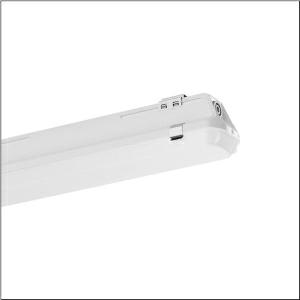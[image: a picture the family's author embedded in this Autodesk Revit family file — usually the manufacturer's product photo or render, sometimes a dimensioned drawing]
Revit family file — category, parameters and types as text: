
# Revit family: monsun_r__11_51fp10mp4b0q_f78f
name_source: partatom
category: Lighting Fixtures
units: mm (PartAtom-declared; Revit-internal decimal feet)

## family parameters
Cut with Voids When Loaded = No
Host = Face
Light Source = No
Part Type = Normal
Room Calculation Point = No
Round Connector Dimension = Use Diameter
Shared = No

## types (1)
- --- (1 x LED, 12070 lm, 66.2 W, 4000K)
    Apparent Load = 66 VA
    CIE Flux Codes = 47 76 93 94 100
    Color Rendering = 80
    Color Temperature = 4000K
    Default Elevation = 1800 mm
    Description = Monsun® 11, damp-proof luminaire, chain hanger, primary optical cover: enclosure, of PMMA, light emission: direct distribution, primary light characteristic: symmetric, installation type: suspended mounting, surface-mounted, horizontal mounting, vertical mounting, LED, rated luminous flux: 12.070lm, luminous efficacy: 182lm/W, light colour: 840, colour temperature: 4000K, control gear: ECG, with terminal, 3-pole, max. 2.5mm², mains connection: 220..240V, AC, 50/60Hz, rated input power: 66W, luminaire housing, of glass-fibre reinforced polyester, uncoated, bright grey, incl. chain hanger, length: 1.590mm, width: 90mm, height: 88mm, clip for enclosure, of stainless steel (V2A), ceiling mounting element, of stainless steel (V2A), chain hanger, of stainless steel (V2A), protection rating (complete): IP66, insulation class (complete): insulation class I (protective earthing), certification: CE, ENEC, VDE, UKCA, protection symbol: D, impact resistance: IK04, permissible operating ambient temperature: -35..+35°C, standard: EN 50419, EN 60598-2-1, no direct snow, no direct sun, no direct rain, for indoor or canopied outdoor use, corresponds to IFS (International Featured Standards) requirements for safety and quality in the food industry, contact your sales advisor before using the luminaires in applications with unclear chemical exposure, large temperature fluctuations or condensation-forming humidity, LABS conformity tested according to VDMA 24364:2018-05, packaging unit: 1 piece
    Height = 89 mm
    Lamp = 1 x LED
    Lamp Light Flux = 12070 lm
    Lamp Power = 66.2 W
    Lamp count = 1
    Length = 1590 mm
    Luminous efficacy = 182 lm/W
    Manufacturer = Siteco
    ModVariant = No
    Model = 51FP10MP4B0Q
    Mounting Place = Ceiling
    Mounting Type = Surface mounted
    Number of Poles = 1
    OnlyDefault = Yes
    Power Factor = 1
    Product Name = Monsun® 11
    Product group = damp-proof luminaire
    ProductGroupID = 300
    Protection Class = Protection class I
    Protection Degree = IP 66
    RLX_Detail_Level = 1
    RLX_Emergency_Light_Flux = 0 lm
    RLX_Emergency_Type = 0
    RLX_Emergency_Type_DB = No
    RlxData = <blob elided: 89805 chars, md5=77497248>
    Socket = socket
    Standby Power = 0 W
    System Light Flux = 12070 lm
    System Power = 66 W
    Type Comments = factory setting: luminous flux: 100 % | (A | C | E) | 155 mA
    Type Image = l_1004748.jpg
    URL = http://relux.com
    VarID = @adj_142091
    Voltage = 0 V
    Weight = 0.00 kg
    Width = 90 mm

## geometry (parser evidence)
native form markers: Blend x4, Sweep x13
no freeform markers — native parametric forms only
